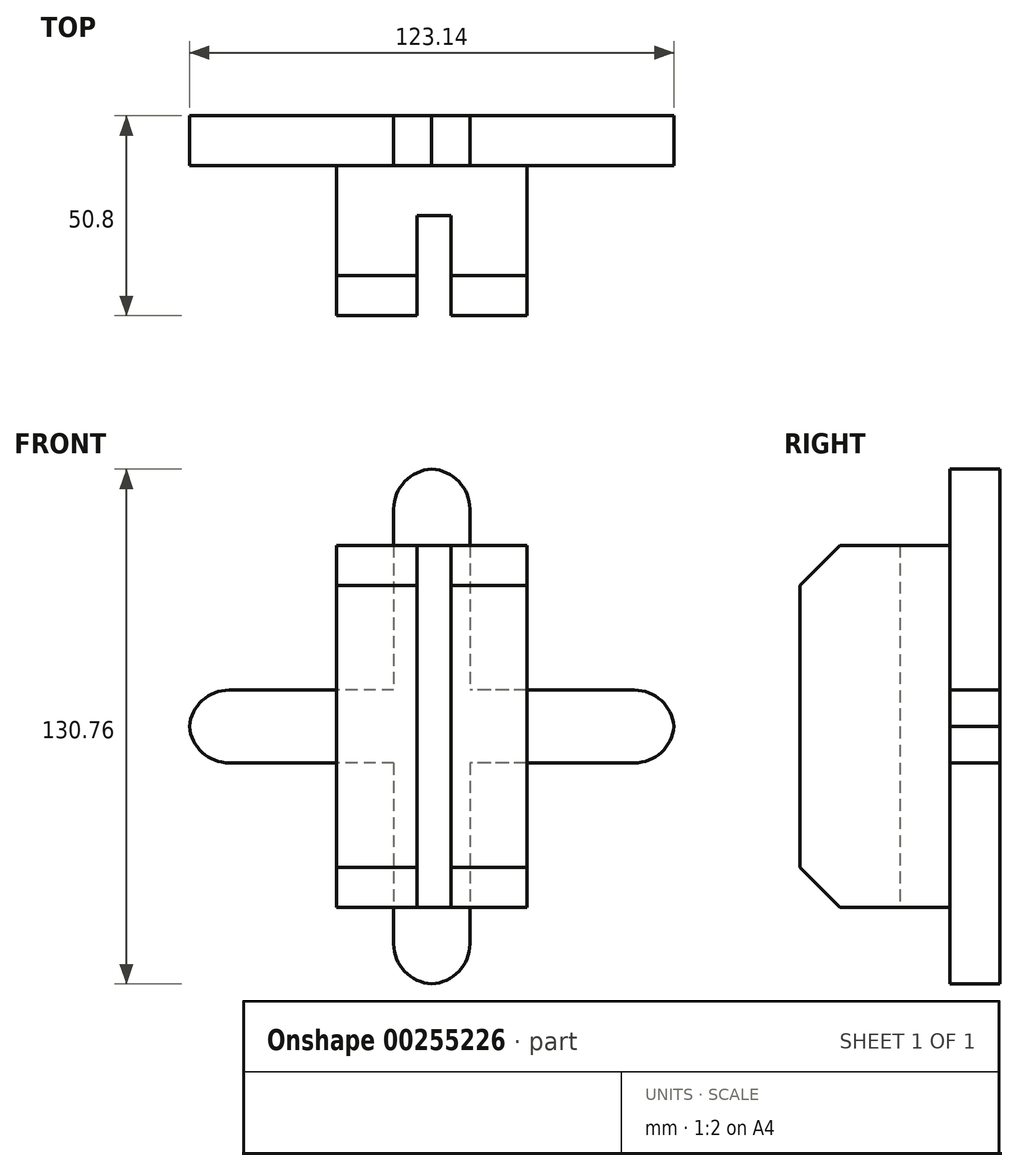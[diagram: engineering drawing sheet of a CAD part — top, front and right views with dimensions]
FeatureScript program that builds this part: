
annotation { "Feature Type Name" : "Feature", "Feature Type Description" : "" }
export const myFeature = defineFeature(function(context is Context, id is Id, definition is map)
    precondition{}
    {
        {
            var Q0;
            Q0=qCreatedBy(makeId("Front.planeOp"),FACE);
            var sketch = newSketch(context, id + "F0", { "sketchPlane" : qUnion([Q0])});
            skLineSegment(sketch, "E0.bottom", {"start": v(9.67, 65.4) * mm, "end": v(-9.67, 65.4) * mm});
            skLineSegment(sketch, "E0.top", {"start": v(9.67, -65.4) * mm, "end": v(-9.67, -65.4) * mm});
            skLineSegment(sketch, "E0.left", {"start": v(9.67, 65.4) * mm, "end": v(9.67, -65.4) * mm});
            skLineSegment(sketch, "E0.right", {"start": v(-9.67, 65.4) * mm, "end": v(-9.67, -65.4) * mm});
            skPoint(sketch, "E0.middle", {"position": v(0, 0) * mm});
            skLineSegment(sketch, "E1.bottom", {"start": v(61.6, 9.25) * mm, "end": v(-61.6, 9.25) * mm});
            skLineSegment(sketch, "E1.top", {"start": v(61.6, -9.25) * mm, "end": v(-61.6, -9.25) * mm});
            skLineSegment(sketch, "E1.left", {"start": v(61.6, 9.25) * mm, "end": v(61.6, -9.25) * mm});
            skLineSegment(sketch, "E1.right", {"start": v(-61.6, 9.25) * mm, "end": v(-61.6, -9.25) * mm});
            skSolve(sketch);
        }
        {
            var Q0;
            Q0 = qSketchRegion(id + "F0", true);
            extrude(context, id + "F1", {"entities" : qUnion([Q0]), "depth" : 12.7 * mm});
        }
        {
            var Q0;
            Q0=makeQuery(id+"F1.opExtrude","SWEPT_EDGE",EDGE,{"disambiguationData":[OSD([sQuery(id+"F0.wireOp",EDGE,"E0.bottom"),sQuery(id+"F0.wireOp",EDGE,"E0.left")])]});
            var Q1;
            Q1=makeQuery(id+"F1.opExtrude","SWEPT_EDGE",EDGE,{"disambiguationData":[OSD([sQuery(id+"F0.wireOp",EDGE,"E0.bottom"),sQuery(id+"F0.wireOp",EDGE,"E0.right")])]});
            var Q2;
            Q2=makeQuery(id+"F1.opExtrude","SWEPT_EDGE",EDGE,{"disambiguationData":[OSD([sQuery(id+"F0.wireOp",EDGE,"E1.bottom"),sQuery(id+"F0.wireOp",EDGE,"E1.left")])]});
            var Q3;
            Q3=makeQuery(id+"F1.opExtrude","SWEPT_EDGE",EDGE,{"disambiguationData":[OSD([sQuery(id+"F0.wireOp",EDGE,"E1.top"),sQuery(id+"F0.wireOp",EDGE,"E1.left")])]});
            var Q4;
            Q4=makeQuery(id+"F1.opExtrude","SWEPT_EDGE",EDGE,{"disambiguationData":[OSD([sQuery(id+"F0.wireOp",EDGE,"E0.top"),sQuery(id+"F0.wireOp",EDGE,"E0.left")])]});
            var Q5;
            Q5=makeQuery(id+"F1.opExtrude","SWEPT_EDGE",EDGE,{"disambiguationData":[OSD([sQuery(id+"F0.wireOp",EDGE,"E1.bottom"),sQuery(id+"F0.wireOp",EDGE,"E1.right")])]});
            var Q6;
            Q6=makeQuery(id+"F1.opExtrude","SWEPT_EDGE",EDGE,{"disambiguationData":[OSD([sQuery(id+"F0.wireOp",EDGE,"E1.top"),sQuery(id+"F0.wireOp",EDGE,"E1.right")])]});
            var Q7;
            Q7=makeQuery(id+"F1.opExtrude","SWEPT_EDGE",EDGE,{"disambiguationData":[OSD([sQuery(id+"F0.wireOp",EDGE,"E0.top"),sQuery(id+"F0.wireOp",EDGE,"E0.right")])]});
            fillet(context, id + "F2", {"entities" : qUnion([Q0, Q1, Q2, Q3, Q4, Q5, Q6, Q7]), "radius" : 10.16 * mm, "tangentPropagation" : true, "allowEdgeOverflow" : false});
        }
        {
            var Q0;
            Q0=makeQuery(id+"F1.opExtrude","CAP_FACE",FACE,{"disambiguationData":[OSD([sQuery(id+"F0.wireOp",EDGE,"E0.bottom"),sQuery(id+"F0.wireOp",EDGE,"E0.top"),sQuery(id+"F0.wireOp",EDGE,"E0.left"),sQuery(id+"F0.wireOp",EDGE,"E0.right"),sQuery(id+"F0.wireOp",EDGE,"E1.bottom"),sQuery(id+"F0.wireOp",EDGE,"E1.top"),sQuery(id+"F0.wireOp",EDGE,"E1.left"),sQuery(id+"F0.wireOp",EDGE,"E1.right")])],"isStart":false});
            var sketch = newSketch(context, id + "F3", { "sketchPlane" : qUnion([Q0])});
            skLineSegment(sketch, "E2.bottom", {"start": v(24.21, 45.96) * mm, "end": v(-24.21, 45.96) * mm});
            skLineSegment(sketch, "E2.top", {"start": v(24.21, -45.96) * mm, "end": v(-24.21, -45.96) * mm});
            skLineSegment(sketch, "E2.left", {"start": v(24.21, 45.96) * mm, "end": v(24.21, -45.96) * mm});
            skLineSegment(sketch, "E2.right", {"start": v(-24.21, 45.96) * mm, "end": v(-24.21, -45.96) * mm});
            skPoint(sketch, "E2.middle", {"position": v(0, 0) * mm});
            skSolve(sketch);
        }
        {
            var Q0;
            Q0 = qSketchRegion(id + "F3", true);
            extrude(context, id + "F4", {"entities" : qUnion([Q0]), "operationType" : NewBodyOperationType.ADD, "depth" : 12.7 * mm});
        }
        {
            var Q0;
            Q0=makeQuery(id+"F4.opExtrude","CAP_FACE",FACE,{"disambiguationData":[OSD([sQuery(id+"F3.wireOp",EDGE,"E2.bottom"),sQuery(id+"F3.wireOp",EDGE,"E2.top"),sQuery(id+"F3.wireOp",EDGE,"E2.left"),sQuery(id+"F3.wireOp",EDGE,"E2.right")])],"isStart":false});
            var sketch = newSketch(context, id + "F5", { "sketchPlane" : qUnion([Q0])});
            skLineSegment(sketch, "E3.bottom", {"start": v(-24.21, 45.96) * mm, "end": v(-3.77, 45.96) * mm});
            skLineSegment(sketch, "E3.top", {"start": v(-24.21, -45.96) * mm, "end": v(-3.77, -45.96) * mm});
            skLineSegment(sketch, "E3.left", {"start": v(-24.21, 45.96) * mm, "end": v(-24.21, -45.96) * mm});
            skLineSegment(sketch, "E3.right", {"start": v(-3.77, 45.96) * mm, "end": v(-3.77, -45.96) * mm});
            skLineSegment(sketch, "E4.bottom", {"start": v(24.21, 45.96) * mm, "end": v(4.92, 45.96) * mm});
            skLineSegment(sketch, "E4.top", {"start": v(24.21, -45.96) * mm, "end": v(4.92, -45.96) * mm});
            skLineSegment(sketch, "E4.left", {"start": v(24.21, 45.96) * mm, "end": v(24.21, -45.96) * mm});
            skLineSegment(sketch, "E4.right", {"start": v(4.92, 45.96) * mm, "end": v(4.92, -45.96) * mm});
            skSolve(sketch);
        }
        {
            var Q0;
            Q0 = qSketchRegion(id + "F5", true);
            extrude(context, id + "F6", {"entities" : qUnion([Q0]), "operationType" : NewBodyOperationType.ADD, "depth" : 25.4 * mm});
        }
        {
            var Q0;
            Q0=makeQuery(id+"F6.opExtrude","CAP_EDGE",EDGE,{"disambiguationData":[OSD([sQuery(id+"F5.wireOp",EDGE,"E3.bottom")])],"isStart":false});
            var Q1;
            Q1=makeQuery(id+"F6.opExtrude","CAP_EDGE",EDGE,{"disambiguationData":[OSD([sQuery(id+"F5.wireOp",EDGE,"E3.top")])],"isStart":false});
            var Q2;
            Q2=makeQuery(id+"F6.opExtrude","CAP_EDGE",EDGE,{"disambiguationData":[OSD([sQuery(id+"F5.wireOp",EDGE,"E4.top")])],"isStart":false});
            var Q3;
            Q3=makeQuery(id+"F6.opExtrude","CAP_EDGE",EDGE,{"disambiguationData":[OSD([sQuery(id+"F5.wireOp",EDGE,"E4.bottom")])],"isStart":false});
            chamfer(context, id + "F7", {"entities" : qUnion([Q0, Q1, Q2, Q3]), "width" : 10.16 * mm, "tangentPropagation" : true});
        }
    });
